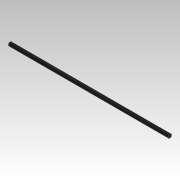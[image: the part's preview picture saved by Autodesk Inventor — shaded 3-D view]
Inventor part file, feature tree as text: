
AUTODESK INVENTOR PART (.ipt)
format: ipt  version: 2020 (Build 240168000, 168)  size: 90,624 bytes
history: native  units: mm
features: revolve x1, chamfer x1, sketch x1
ambient origin geometry x8: Origin, YZ Plane, XZ Plane, XY Plane, X Axis, Y Axis, Z Axis, Center Point
bodies: Solid1 (feature_tree)
feature tree (3):
  revolve  "Revolution1"  [1 undecoded]
  chamfer  "Chamfer1"  Distance=250.0mm
  sketch  "Sketch1"  dims[d0=2.0mm d1=3.0mm d2=250.0mm d3=90.0deg d4=0.5mm d5=2.0mm d6=45.0deg]
note: 1 required parameter value undecoded (feature->parameter linkage not recoverable at this tier; creation-order binding heuristic only, values carry confidence <= 0.55)
